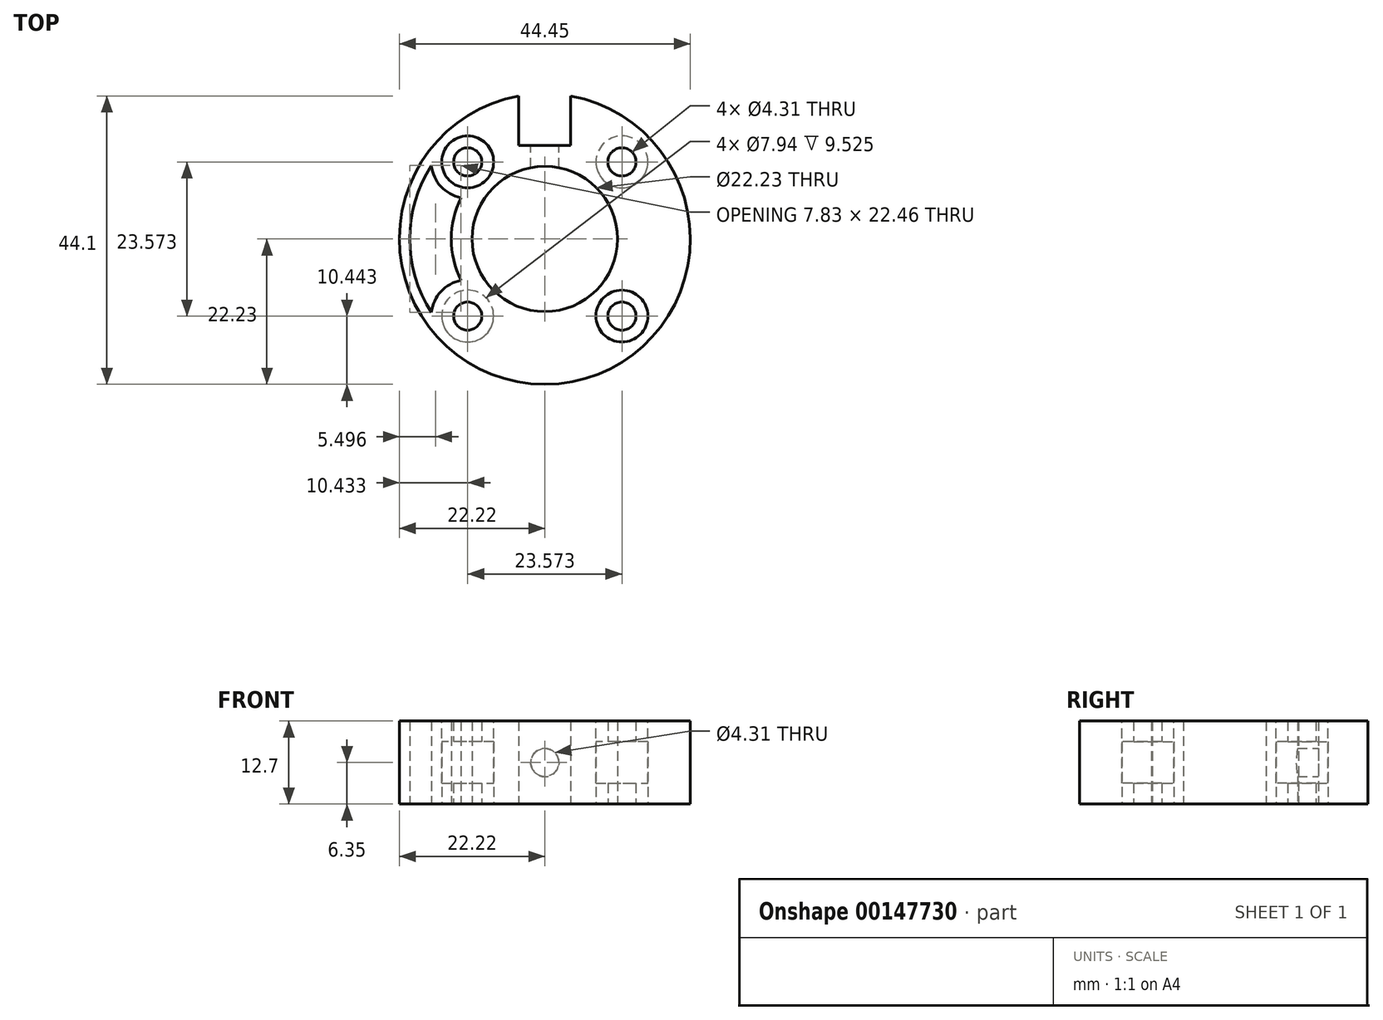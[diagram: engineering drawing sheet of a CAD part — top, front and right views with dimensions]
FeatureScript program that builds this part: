
annotation { "Feature Type Name" : "Feature", "Feature Type Description" : "" }
export const myFeature = defineFeature(function(context is Context, id is Id, definition is map)
    precondition{}
    {
        {
            var Q0;
            Q0=qCreatedBy(makeId("Top.planeOp"),FACE);
            var sketch = newSketch(context, id + "F0", { "sketchPlane" : qUnion([Q0])});
            skCircle(sketch, "E0", {"center": v(0, 0) * mm, "radius": 11.11 * mm});
            skLineSegment(sketch, "E1.bottom", {"start": v(11.79, 11.79) * mm, "end": v(-11.79, 11.79) * mm, "construction": true});
            skLineSegment(sketch, "E1.top", {"start": v(11.79, -11.79) * mm, "end": v(-11.79, -11.79) * mm, "construction": true});
            skLineSegment(sketch, "E1.left", {"start": v(11.79, 11.79) * mm, "end": v(11.79, -11.79) * mm, "construction": true});
            skLineSegment(sketch, "E1.right", {"start": v(-11.79, 11.79) * mm, "end": v(-11.79, -11.79) * mm, "construction": true});
            skCircle(sketch, "E2", {"center": v(-11.79, 11.79) * mm, "radius": 5.56 * mm, "construction": true});
            skLineSegment(sketch, "E3", {"start": v(0, 0) * mm, "end": v(0, 11.11) * mm});
            skLineSegment(sketch, "E4", {"start": v(0, 11.11) * mm, "end": v(0, 14.29) * mm});
            skLineSegment(sketch, "E5.bottom", {"start": v(-3.97, 21.87) * mm, "end": v(3.97, 21.87) * mm, "construction": true});
            skLineSegment(sketch, "E5.top", {"start": v(-3.97, 14.29) * mm, "end": v(3.97, 14.29) * mm});
            skLineSegment(sketch, "E5.left", {"start": v(-3.97, 21.87) * mm, "end": v(-3.97, 14.29) * mm});
            skLineSegment(sketch, "E5.right", {"start": v(3.97, 21.87) * mm, "end": v(3.97, 14.29) * mm});
            skArc(sketch, "E6", {"start": v(-3.97, 21.87) * mm, "mid": v(0, -22.22) * mm, "end": v(3.97, 21.87) * mm});
            skCircle(sketch, "E7", {"center": v(-11.79, 11.79) * mm, "radius": 2.15 * mm});
            skCircle(sketch, "E8", {"center": v(-11.79, -11.79) * mm, "radius": 2.15 * mm});
            skCircle(sketch, "E9", {"center": v(11.79, -11.79) * mm, "radius": 2.15 * mm});
            skCircle(sketch, "E10", {"center": v(11.79, 11.79) * mm, "radius": 2.15 * mm});
            skSolve(sketch);
        }
        {
            var Q0;
            Q0=qSketchRegion(id+"F0",true);
            extrude(context, id + "F1", {"entities" : qUnion([Q0]), "depth" : 12.7 * mm});
        }
        {
            var Q0;
            Q0=makeQuery(id+"F1.opExtrude","SWEPT_FACE",FACE,{"disambiguationData":[OSD([sQuery(id+"F0.wireOp",EDGE,"E5.top")])]});
            var sketch = newSketch(context, id + "F2", { "sketchPlane" : qUnion([Q0])});
            skLineSegment(sketch, "E11", {"start": v(0, 12.7) * mm, "end": v(0, 0) * mm, "construction": true});
            skCircle(sketch, "E12", {"center": v(0, 6.35) * mm, "radius": 2.15 * mm});
            skSolve(sketch);
        }
        {
            var Q0;
            Q0=qSketchRegion(id+"F2",true);
            var Q1;
            Q1=makeQuery(id+"F1.opExtrude","SWEPT_FACE",FACE,{"disambiguationData":[OSD([sQuery(id+"F0.wireOp",EDGE,"E0")])]});
            extrude(context, id + "F3", {"entities" : qUnion([Q0]), "operationType" : NewBodyOperationType.REMOVE, "endBound" : BoundingType.UP_TO_SURFACE, "oppositeDirection" : true, "endBoundEntityFace" : qUnion([Q1]), "depth" : 25.4 * mm});
        }
        {
            var Q0;
            Q0=makeQuery(id+"F1.opExtrude","CAP_FACE",FACE,{"disambiguationData":[OSD([sQuery(id+"F0.wireOp",EDGE,"E0"),sQuery(id+"F0.wireOp",EDGE,"E5.top"),sQuery(id+"F0.wireOp",EDGE,"E5.left"),sQuery(id+"F0.wireOp",EDGE,"E5.right"),sQuery(id+"F0.wireOp",EDGE,"E6"),sQuery(id+"F0.wireOp",EDGE,"E7"),sQuery(id+"F0.wireOp",EDGE,"E8"),sQuery(id+"F0.wireOp",EDGE,"E9"),sQuery(id+"F0.wireOp",EDGE,"E10")])],"isStart":true});
            cPlane(context, id + "F4", {"entities" : qUnion([Q0]), "cplaneType" : CPlaneType.OFFSET, "offset" : 3.17 * mm, "oppositeDirection" : true, "width" : 152.4 * mm, "height" : 152.4 * mm});
        }
        {
            var Q0;
            Q0=makeQuery(id+"F1.opExtrude","CAP_FACE",FACE,{"disambiguationData":[OSD([sQuery(id+"F0.wireOp",EDGE,"E0"),sQuery(id+"F0.wireOp",EDGE,"E5.top"),sQuery(id+"F0.wireOp",EDGE,"E5.left"),sQuery(id+"F0.wireOp",EDGE,"E5.right"),sQuery(id+"F0.wireOp",EDGE,"E6"),sQuery(id+"F0.wireOp",EDGE,"E7"),sQuery(id+"F0.wireOp",EDGE,"E8"),sQuery(id+"F0.wireOp",EDGE,"E9"),sQuery(id+"F0.wireOp",EDGE,"E10")])],"isStart":false});
            cPlane(context, id + "F5", {"entities" : qUnion([Q0]), "cplaneType" : CPlaneType.OFFSET, "offset" : 3.17 * mm, "oppositeDirection" : true, "width" : 152.4 * mm, "height" : 152.4 * mm});
        }
        {
            var Q0;
            Q0=makeQuery(id+"F1.opExtrude","CAP_FACE",FACE,{"disambiguationData":[OSD([sQuery(id+"F0.wireOp",EDGE,"E0"),sQuery(id+"F0.wireOp",EDGE,"E5.top"),sQuery(id+"F0.wireOp",EDGE,"E5.left"),sQuery(id+"F0.wireOp",EDGE,"E5.right"),sQuery(id+"F0.wireOp",EDGE,"E6"),sQuery(id+"F0.wireOp",EDGE,"E7"),sQuery(id+"F0.wireOp",EDGE,"E8"),sQuery(id+"F0.wireOp",EDGE,"E9"),sQuery(id+"F0.wireOp",EDGE,"E10")])],"isStart":true});
            var sketch = newSketch(context, id + "F6", { "sketchPlane" : qUnion([Q0])});
            skCircle(sketch, "E13", {"center": v(11.79, -11.79) * mm, "radius": 3.97 * mm});
            skCircle(sketch, "E14", {"center": v(-11.79, 11.79) * mm, "radius": 3.97 * mm});
            skSolve(sketch);
        }
        {
            var Q0;
            Q0=qSketchRegion(id+"F6",true);
            var Q1;
            Q1=qCreatedBy(id+"F5.planeOp",FACE);
            extrude(context, id + "F7", {"entities" : qUnion([Q0]), "operationType" : NewBodyOperationType.REMOVE, "endBound" : BoundingType.UP_TO_SURFACE, "oppositeDirection" : true, "endBoundEntityFace" : qUnion([Q1]), "depth" : 25.4 * mm});
        }
        {
            var Q0;
            Q0=makeQuery(id+"F1.opExtrude","CAP_FACE",FACE,{"disambiguationData":[OSD([sQuery(id+"F0.wireOp",EDGE,"E0"),sQuery(id+"F0.wireOp",EDGE,"E5.top"),sQuery(id+"F0.wireOp",EDGE,"E5.left"),sQuery(id+"F0.wireOp",EDGE,"E5.right"),sQuery(id+"F0.wireOp",EDGE,"E6"),sQuery(id+"F0.wireOp",EDGE,"E7"),sQuery(id+"F0.wireOp",EDGE,"E8"),sQuery(id+"F0.wireOp",EDGE,"E9"),sQuery(id+"F0.wireOp",EDGE,"E10")])],"isStart":true});
            var sketch = newSketch(context, id + "F8", { "sketchPlane" : qUnion([Q0])});
            skArc(sketch, "E15", {"start": v(-12.81, -6.33) * mm, "mid": v(-15.88, -8.03) * mm, "end": v(-17.31, -11.23) * mm});
            skArc(sketch, "E16", {"start": v(-17.31, 11.23) * mm, "mid": v(-15.88, 8.03) * mm, "end": v(-12.81, 6.33) * mm});
            skArc(sketch, "E17", {"start": v(-17.31, 11.23) * mm, "mid": v(-20.64, 0) * mm, "end": v(-17.31, -11.23) * mm});
            skArc(sketch, "E18", {"start": v(-12.81, 6.33) * mm, "mid": v(-14.29, 0) * mm, "end": v(-12.81, -6.33) * mm});
            skSolve(sketch);
        }
        {
            var Q0;
            Q0=qSketchRegion(id+"F8",true);
            var Q1;
            Q1=makeQuery(id+"F1.opExtrude","CAP_FACE",FACE,{"disambiguationData":[OSD([sQuery(id+"F0.wireOp",EDGE,"E0"),sQuery(id+"F0.wireOp",EDGE,"E5.top"),sQuery(id+"F0.wireOp",EDGE,"E5.left"),sQuery(id+"F0.wireOp",EDGE,"E5.right"),sQuery(id+"F0.wireOp",EDGE,"E6"),sQuery(id+"F0.wireOp",EDGE,"E7"),sQuery(id+"F0.wireOp",EDGE,"E8"),sQuery(id+"F0.wireOp",EDGE,"E9"),sQuery(id+"F0.wireOp",EDGE,"E10")])],"isStart":false});
            extrude(context, id + "F9", {"entities" : qUnion([Q0]), "operationType" : NewBodyOperationType.REMOVE, "endBound" : BoundingType.UP_TO_SURFACE, "oppositeDirection" : true, "endBoundEntityFace" : qUnion([Q1]), "depth" : 25.4 * mm});
        }
        {
            var Q0;
            Q0=makeQuery(id+"F1.opExtrude","CAP_FACE",FACE,{"disambiguationData":[OSD([sQuery(id+"F0.wireOp",EDGE,"E0"),sQuery(id+"F0.wireOp",EDGE,"E5.top"),sQuery(id+"F0.wireOp",EDGE,"E5.left"),sQuery(id+"F0.wireOp",EDGE,"E5.right"),sQuery(id+"F0.wireOp",EDGE,"E6"),sQuery(id+"F0.wireOp",EDGE,"E7"),sQuery(id+"F0.wireOp",EDGE,"E8"),sQuery(id+"F0.wireOp",EDGE,"E9"),sQuery(id+"F0.wireOp",EDGE,"E10")])],"isStart":false});
            var sketch = newSketch(context, id + "F10", { "sketchPlane" : qUnion([Q0])});
            skCircle(sketch, "E19", {"center": v(11.79, -11.79) * mm, "radius": 3.97 * mm});
            skCircle(sketch, "E20", {"center": v(-11.79, 11.79) * mm, "radius": 3.97 * mm});
            skSolve(sketch);
        }
        {
            var Q0;
            Q0=qSketchRegion(id+"F10",true);
            var Q1;
            Q1=qCreatedBy(id+"F4.planeOp",FACE);
            extrude(context, id + "F11", {"entities" : qUnion([Q0]), "operationType" : NewBodyOperationType.REMOVE, "endBound" : BoundingType.UP_TO_SURFACE, "oppositeDirection" : true, "endBoundEntityFace" : qUnion([Q1]), "depth" : 25.4 * mm});
        }
    });
